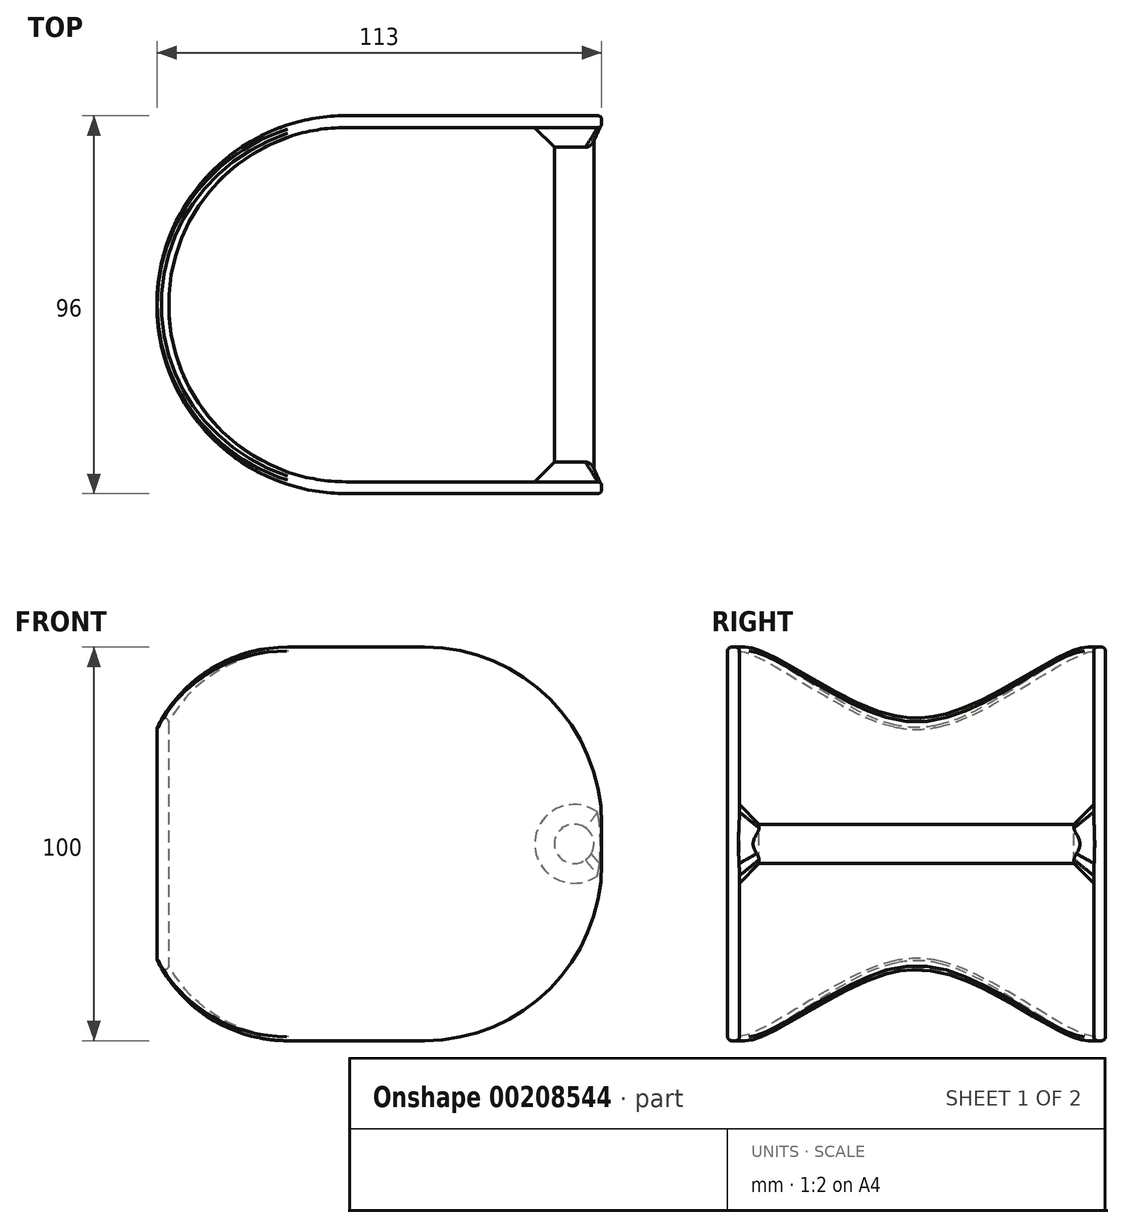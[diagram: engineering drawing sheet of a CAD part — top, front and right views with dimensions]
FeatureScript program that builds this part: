
annotation { "Feature Type Name" : "Feature", "Feature Type Description" : "" }
export const myFeature = defineFeature(function(context is Context, id is Id, definition is map)
    precondition{}
    {
        {
            var Q0;
            Q0=qCreatedBy(makeId("Top.planeOp"),FACE);
            var sketch = newSketch(context, id + "F0", { "sketchPlane" : qUnion([Q0])});
            skCircle(sketch, "E0", {"center": v(0, 0) * mm, "radius": 48 * mm});
            skLineSegment(sketch, "E1", {"start": v(0, 48) * mm, "end": v(65, 48) * mm});
            skLineSegment(sketch, "E2", {"start": v(0, -48) * mm, "end": v(65, -48) * mm});
            skCircle(sketch, "E3", {"center": v(0, 0) * mm, "radius": 45 * mm});
            skLineSegment(sketch, "E4", {"start": v(0, 45) * mm, "end": v(65, 45) * mm});
            skLineSegment(sketch, "E5", {"start": v(0, -45) * mm, "end": v(65, -45) * mm});
            skLineSegment(sketch, "E6", {"start": v(65, -45) * mm, "end": v(65, -48) * mm});
            skLineSegment(sketch, "E7", {"start": v(65, 45) * mm, "end": v(65, 48) * mm});
            skSolve(sketch);
        }
        {
            var Q0;
            {var subQ0=sQuery(id+"F0.wireOp",EDGE,"E1");Q0=makeQuery(id+"F0.imprint","IMPRINT",FACE,{"disambiguationData":[TD([[makeQuery(id+"F0.imprint","IMPRINT",EDGE,{"derivedFrom":subQ0}),-1.0]])]});}
            var Q1;
            {var subQ0=sQuery(id+"F0.wireOp",EDGE,"E0");var subQ8=makeQuery(id+"F0.imprint","INTERSECT",VERTEX,{"derivedFrom":[subQ0,sQuery(id+"F0.wireOp",EDGE,"E1")]});Q1=makeQuery(id+"F0.imprint","IMPRINT",FACE,{"disambiguationData":[TD([[makeQuery(id+"F0.imprint","IMPRINT",EDGE,{"disambiguationData":[TD([[subQ8,1.0]])],"derivedFrom":subQ0}),1.0]])]});}
            var Q2;
            {var subQ0=sQuery(id+"F0.wireOp",EDGE,"E2");Q2=makeQuery(id+"F0.imprint","IMPRINT",FACE,{"disambiguationData":[TD([[makeQuery(id+"F0.imprint","IMPRINT",EDGE,{"derivedFrom":subQ0}),1.0]])]});}
            extrude(context, id + "F1", {"entities" : qUnion([Q0, Q1, Q2]), "depth" : 100 * mm});
        }
        {
            var Q0;
            Q0=makeQuery(id+"F1.opExtrude","CAP_EDGE",EDGE,{"disambiguationData":[OSD([sQuery(id+"F0.wireOp",EDGE,"E7")])],"isStart":false});
            var Q1;
            Q1=makeQuery(id+"F1.opExtrude","CAP_EDGE",EDGE,{"disambiguationData":[OSD([sQuery(id+"F0.wireOp",EDGE,"E7")])],"isStart":true});
            var Q2;
            Q2=makeQuery(id+"F1.opExtrude","CAP_EDGE",EDGE,{"disambiguationData":[OSD([sQuery(id+"F0.wireOp",EDGE,"E6")])],"isStart":true});
            var Q3;
            Q3=makeQuery(id+"F1.opExtrude","CAP_EDGE",EDGE,{"disambiguationData":[OSD([sQuery(id+"F0.wireOp",EDGE,"E6")])],"isStart":false});
            fillet(context, id + "F2", {"entities" : qUnion([Q0, Q1, Q2, Q3]), "radius" : 45 * mm, "tangentPropagation" : true, "allowEdgeOverflow" : false});
        }
        {
            var Q0;
            Q0=qCreatedBy(makeId("Front.planeOp"),FACE);
            var sketch = newSketch(context, id + "F3", { "sketchPlane" : qUnion([Q0])});
            skCircle(sketch, "E8", {"center": v(10, 50) * mm, "radius": 65 * mm});
            skCircle(sketch, "E9", {"center": v(58, 50) * mm, "radius": 5 * mm});
            skCircle(sketch, "E10", {"center": v(10, 50) * mm, "radius": 89.77 * mm});
            skLineSegment(sketch, "E11", {"start": v(0, 150.25) * mm, "end": v(0, -57.97) * mm});
            skSolve(sketch);
        }
        {
            var Q0;
            {var subQ0=sQuery(id+"F3.wireOp",EDGE,"E11");var subQ1=sQuery(id+"F3.wireOp",EDGE,"E8");var subQ2=makeQuery(id+"F3.imprint","INTERSECT",VERTEX,{"disambiguationData":[OD(0.0)],"derivedFrom":[subQ1,subQ0]});Q0=makeQuery(id+"F3.imprint","IMPRINT",FACE,{"disambiguationData":[TD([[makeQuery(id+"F3.imprint","IMPRINT",EDGE,{"disambiguationData":[TD([[subQ2,-1.0]])],"derivedFrom":subQ1}),-1.0]])]});}
            extrude(context, id + "F4", {"entities" : qUnion([Q0]), "operationType" : NewBodyOperationType.REMOVE, "oppositeDirection" : true, "depth" : 100 * mm, "symmetric" : true});
        }
        {
            var Q0;
            Q0=makeQuery(id+"F3.imprint","IMPRINT",FACE,{"disambiguationData":[TD([[makeQuery(id+"F3.imprint","IMPRINT",EDGE,{"derivedFrom":sQuery(id+"F3.wireOp",EDGE,"E9")}),1.0]])]});
            extrude(context, id + "F5", {"entities" : qUnion([Q0]), "operationType" : NewBodyOperationType.ADD, "depth" : 96 * mm, "symmetric" : true});
        }
        {
            var Q0;
            Q0=makeQuery(id+"F4.boolean.opBoolean","INTERSECT",EDGE,{"disambiguationData":[OD(0.0)],"derivedFrom":[makeQuery(id+"F1.opExtrude","CAP_FACE",FACE,{"disambiguationData":[OSD([sQuery(id+"F0.wireOp",EDGE,"E0"),sQuery(id+"F0.wireOp",EDGE,"E1"),sQuery(id+"F0.wireOp",EDGE,"E2"),sQuery(id+"F0.wireOp",EDGE,"E3"),sQuery(id+"F0.wireOp",EDGE,"E4"),sQuery(id+"F0.wireOp",EDGE,"E5"),sQuery(id+"F0.wireOp",EDGE,"E6"),sQuery(id+"F0.wireOp",EDGE,"E7")])],"isStart":true}),makeQuery(id+"F4.opExtrude","SWEPT_FACE",FACE,{"disambiguationData":[OSD([sQuery(id+"F3.wireOp",EDGE,"E8")])]})]});
            var Q1;
            Q1=makeQuery(id+"F4.boolean.opBoolean","INTERSECT",EDGE,{"disambiguationData":[OD(0.0)],"derivedFrom":[makeQuery(id+"F1.opExtrude","CAP_FACE",FACE,{"disambiguationData":[OSD([sQuery(id+"F0.wireOp",EDGE,"E0"),sQuery(id+"F0.wireOp",EDGE,"E1"),sQuery(id+"F0.wireOp",EDGE,"E2"),sQuery(id+"F0.wireOp",EDGE,"E3"),sQuery(id+"F0.wireOp",EDGE,"E4"),sQuery(id+"F0.wireOp",EDGE,"E5"),sQuery(id+"F0.wireOp",EDGE,"E6"),sQuery(id+"F0.wireOp",EDGE,"E7")])],"isStart":false}),makeQuery(id+"F4.opExtrude","SWEPT_FACE",FACE,{"disambiguationData":[OSD([sQuery(id+"F3.wireOp",EDGE,"E8")])]})]});
            var Q2;
            Q2=makeQuery(id+"F4.boolean.opBoolean","INTERSECT",EDGE,{"disambiguationData":[OD(1.0)],"derivedFrom":[makeQuery(id+"F1.opExtrude","CAP_FACE",FACE,{"disambiguationData":[OSD([sQuery(id+"F0.wireOp",EDGE,"E0"),sQuery(id+"F0.wireOp",EDGE,"E1"),sQuery(id+"F0.wireOp",EDGE,"E2"),sQuery(id+"F0.wireOp",EDGE,"E3"),sQuery(id+"F0.wireOp",EDGE,"E4"),sQuery(id+"F0.wireOp",EDGE,"E5"),sQuery(id+"F0.wireOp",EDGE,"E6"),sQuery(id+"F0.wireOp",EDGE,"E7")])],"isStart":false}),makeQuery(id+"F4.opExtrude","SWEPT_FACE",FACE,{"disambiguationData":[OSD([sQuery(id+"F3.wireOp",EDGE,"E8")])]})]});
            var Q3;
            Q3=makeQuery(id+"F4.boolean.opBoolean","INTERSECT",EDGE,{"disambiguationData":[OD(1.0)],"derivedFrom":[makeQuery(id+"F1.opExtrude","CAP_FACE",FACE,{"disambiguationData":[OSD([sQuery(id+"F0.wireOp",EDGE,"E0"),sQuery(id+"F0.wireOp",EDGE,"E1"),sQuery(id+"F0.wireOp",EDGE,"E2"),sQuery(id+"F0.wireOp",EDGE,"E3"),sQuery(id+"F0.wireOp",EDGE,"E4"),sQuery(id+"F0.wireOp",EDGE,"E5"),sQuery(id+"F0.wireOp",EDGE,"E6"),sQuery(id+"F0.wireOp",EDGE,"E7")])],"isStart":true}),makeQuery(id+"F4.opExtrude","SWEPT_FACE",FACE,{"disambiguationData":[OSD([sQuery(id+"F3.wireOp",EDGE,"E8")])]})]});
            fillet(context, id + "F6", {"entities" : qUnion([Q0, Q1, Q2, Q3]), "radius" : 37 * mm, "tangentPropagation" : true, "allowEdgeOverflow" : false});
        }
        {
            var Q0;
            {var subQ0=sQuery(id+"F0.wireOp",EDGE,"E7");Q0=makeQuery(id+"F2.opFillet","BLEND_FACE",FACE,{"disambiguationData":[OSD([subQ0]),TDD([makeQuery(id+"F1.opExtrude","CAP_EDGE",EDGE,{"disambiguationData":[OSD([subQ0])],"isStart":true})])]});}
            fillet(context, id + "F7", {"entities" : qUnion([Q0]), "radius" : 1 * mm, "tangentPropagation" : true, "allowEdgeOverflow" : false});
        }
        {
            var Q0;
            Q0=makeQuery(id+"F5.boolean.opBoolean","INTERSECT",EDGE,{"derivedFrom":[makeQuery(id+"F1.opExtrude","SWEPT_FACE",FACE,{"disambiguationData":[OSD([sQuery(id+"F0.wireOp",EDGE,"E4")])]}),makeQuery(id+"F5.opExtrude","SWEPT_FACE",FACE,{"disambiguationData":[OSD([sQuery(id+"F3.wireOp",EDGE,"E9")])]})]});
            var Q1;
            Q1=makeQuery(id+"F5.boolean.opBoolean","INTERSECT",EDGE,{"derivedFrom":[makeQuery(id+"F1.opExtrude","SWEPT_FACE",FACE,{"disambiguationData":[OSD([sQuery(id+"F0.wireOp",EDGE,"E5")])]}),makeQuery(id+"F5.opExtrude","SWEPT_FACE",FACE,{"disambiguationData":[OSD([sQuery(id+"F3.wireOp",EDGE,"E9")])]})]});
            chamfer(context, id + "F8", {"entities" : qUnion([Q0, Q1]), "width" : 5 * mm, "tangentPropagation" : true});
        }
    });
